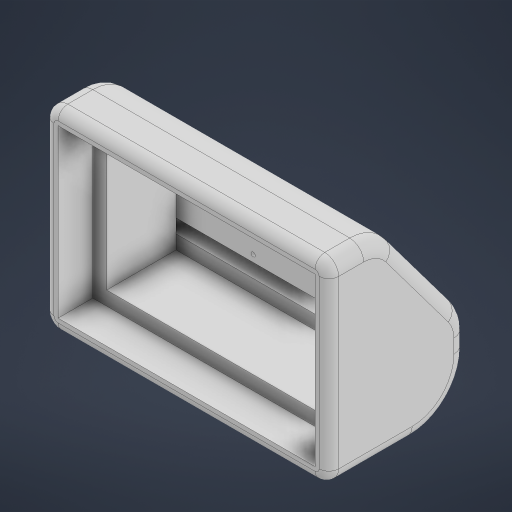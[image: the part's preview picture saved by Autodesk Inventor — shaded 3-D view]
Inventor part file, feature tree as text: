
AUTODESK INVENTOR PART (.ipt)
format: ipt  version: 2023 (Build 270158000, 158)  size: 316,928 bytes
history: native  units: mm
features: extrude x7, sketch x5, fillet x5, chamfer x2
ambient origin geometry x8: Origin, YZ Plane, XZ Plane, XY Plane, X Axis, Y Axis, Z Axis, Center Point
bodies: Solid1 (feature_tree)
feature tree (19):
  sketch  "Sketch1"  dims[d0=185.0mm d1=120.0mm]
  extrude  "Extrusion1"  Depth=120.0mm
  extrude  "Extrusion2"  Depth=10.0mm
  fillet  "Fillet1"  Radius=205.0mm
  chamfer  "Chamfer1"  Distance=100.0mm
  fillet  "Fillet2"  Radius=25.0mm
  fillet  "Fillet3"  Radius=7.0mm
  fillet  "Fillet4"  Radius=30.0mm
  extrude  "Extrusion3"  Depth=10.0mm
  sketch  "Sketch3"  dims[d5=140.0mm d6=100.0mm d7=0.0mm d8=25.0mm d9=0.0mm d10=7.0mm]
  extrude  "Extrusion4"  Depth=3.0mm
  extrude  "Extrusion5"  Depth=3.0mm
  extrude  "Extrusion6"  Depth=25.0mm TaperAngle=0.0deg
  extrude  "Extrusion7"  Depth=10.0mm
  chamfer  "Chamfer2"  Distance=25.0mm
  fillet  "Fillet5"  Radius=25.0mm
  sketch  "Sketch2"  dims[d2=10.0mm d3=10.0mm d4=205.0mm]
  sketch  "Sketch4"  dims[d11=80.0mm d12=60.0mm d13=45.0deg d14=30.0mm]
  sketch  "Sketch5"  dims[d15=40.0mm d16=10.0mm d20=3.0mm d21=3.0mm d22=25.0mm d23=0.0mm d24=10.0mm d25=25.0mm d26=0.0mm d27=25.0mm d28=0.0mm d29=10.0mm d30=25.0mm d31=0.0mm d32=25.0mm d33=0.0mm d34=25.0mm d35=60.0mm d36=45.0deg d37=30.0mm d38=26.994mm d39=53.988mm]
